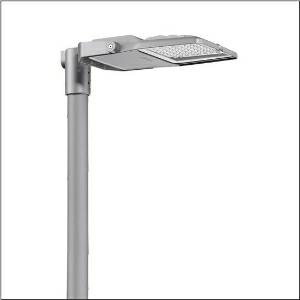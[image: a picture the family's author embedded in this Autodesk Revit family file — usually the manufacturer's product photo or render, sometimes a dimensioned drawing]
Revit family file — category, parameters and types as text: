
# Revit family: floodlight_fl_21_iq_mini___pl33t_5xa7771d4f3a_dbd7
name_source: partatom
category: Lighting Fixtures
units: mm (PartAtom-declared; Revit-internal decimal feet)

## family parameters
Cut with Voids When Loaded = No
Host = Face
Light Source = No
Part Type = Normal
Room Calculation Point = No
Round Connector Dimension = Use Diameter
Shared = No

## types (1)
- --- (1 x LED, 18390 lm, 143 W, 4000K)
    Apparent Load = 143 VA
    CIE Flux Codes = 26 75 99 100 100
    Color Rendering = 70
    Color Temperature = 4000K
    Default Elevation = 1800 mm
    Description = Floodlight FL 21 iQ mini, floodlight, primary light control with lens, of PMMA, primary optical cover: protective disc, of toughened safety glass, transparent, light distribution: PL33T, light emission: direct distribution, installation type: surface-mounted, LED, High Power LED, rated luminous flux: 18.390lm, luminous efficacy: 129lm/W, light colour: 740, colour temperature: 4000K, control gear: iQ Comfort/DALI, control: Auto-Match, Temp-Guard, Lumen-Switch, Night-Set, Smart-Wire, Light-Fading, Desk-Remote (wireless, voltage-free reading and setting of iQ features in the workshop via application-optimized NFC function/RFID function), optimised constant luminous flux control (CLO 2.0), with terminal, 6-pole, mains connection: 220..240V, AC, 50/60Hz, start of lifetime: 143W, end of service life: 152W, reduction: 61W, luminaire housing, of diecast aluminium, powder-coated, Siteco® metallic grey (DB 702S), corrosivity category C5 mid according to DIN EN ISO 12944, suitable for swimming pools, chlorine-resistant, sealing non-destructively replaceable, please order mast flange separately, mast bracket, of steel, galvanised, powder-coated, Siteco® metallic grey (DB 702S), protection rating (complete): IP66, insulation class (complete): insulation class II (safety insulation), certification: CE, ENEC, VDE, protection symbol: D, impact resistance: IK08, permissible operating ambient temperature: -40..+40°C, permissible operating ambient temperature for outdoor applications: -40..+50°C, standard: DIN EN 12944, LABS conformity tested according to VDMA 24364:2018-05, packaging unit: 1 piece

Light Distribution: PL33T
    Height = 70 mm
    Lamp = 1 x LED
    Lamp Light Flux = 18390 lm
    Lamp Power = 143 W
    Lamp count = 1
    Length = 485 mm
    Luminous efficacy = 129 lm/W
    Manufacturer = Siteco
    ModVariant = No
    Model = 5XA7771D4F3A
    Number of Poles = 1
    OnlyDefault = Yes
    Power Factor = 1
    Product Name = Floodlight FL 21 iQ mini | PL33T
    Product group = floodlight | pylon annexe
    ProductGroupID = 6200
    Protection Class = Protection class II
    Protection Degree = IP 66
    RLX_Detail_Level = 1
    RLX_Emergency_Light_Flux = 0 lm
    RLX_Emergency_Type = 0
    RLX_Emergency_Type_DB = No
    RlxData = <blob elided: 101553 chars, md5=5f1ca29d>
    Socket = socket
    Standby Power = 0 W
    System Light Flux = 18390 lm
    System Power = 143 W
    Type Comments = factory setting: luminous flux: 100 % | dim-lin: 254 | 730 mA
    Type Image = l_1007125.jpg
    URL = http://relux.com
    VarID = @adj_149084
    Voltage = 0 V
    Weight = 0.00 kg
    Width = 337 mm

## geometry (parser evidence)
native form markers: Blend x4, Sweep x11
no freeform markers — native parametric forms only
